# Revit family: plankopf_leer
name_source: partatom
category: Planköpfe
units: mm (PartAtom-declared; Revit-internal decimal feet)

## family parameters
Mit Bauteil drehen = Nein

## types (10) — shared parameters

## per-type parameters (varying)
| type | Breite | Höhe |
| a4 | 297 mm  [stored 0.974409 ft] | 210 mm  [stored 0.688976 ft] |
| a1 | 841 mm | 594 mm  [stored 1.94882 ft] |
| a3 | 420 mm  [stored 1.37795 ft] | 297 mm  [stored 0.974409 ft] |
| a2 | 594 mm  [stored 1.94882 ft] | 420 mm  [stored 1.37795 ft] |
| a1 hoch | 594 mm  [stored 1.94882 ft] | 841 mm |
| a2 hoch | 420 mm  [stored 1.37795 ft] | 594 mm  [stored 1.94882 ft] |
| a3 hoch | 297 mm  [stored 0.974409 ft] | 420 mm  [stored 1.37795 ft] |
| a4 hoch | 210 mm  [stored 0.688976 ft] | 297 mm  [stored 0.974409 ft] |
| a0 | 1189 mm  [stored 3.90092 ft] | 841 mm |
| a0 hoch | 841 mm | 1189 mm  [stored 3.90092 ft] |

note: [stored X ft] marks values corroborated as IEEE doubles in the binary element streams (Revit-internal decimal feet)
